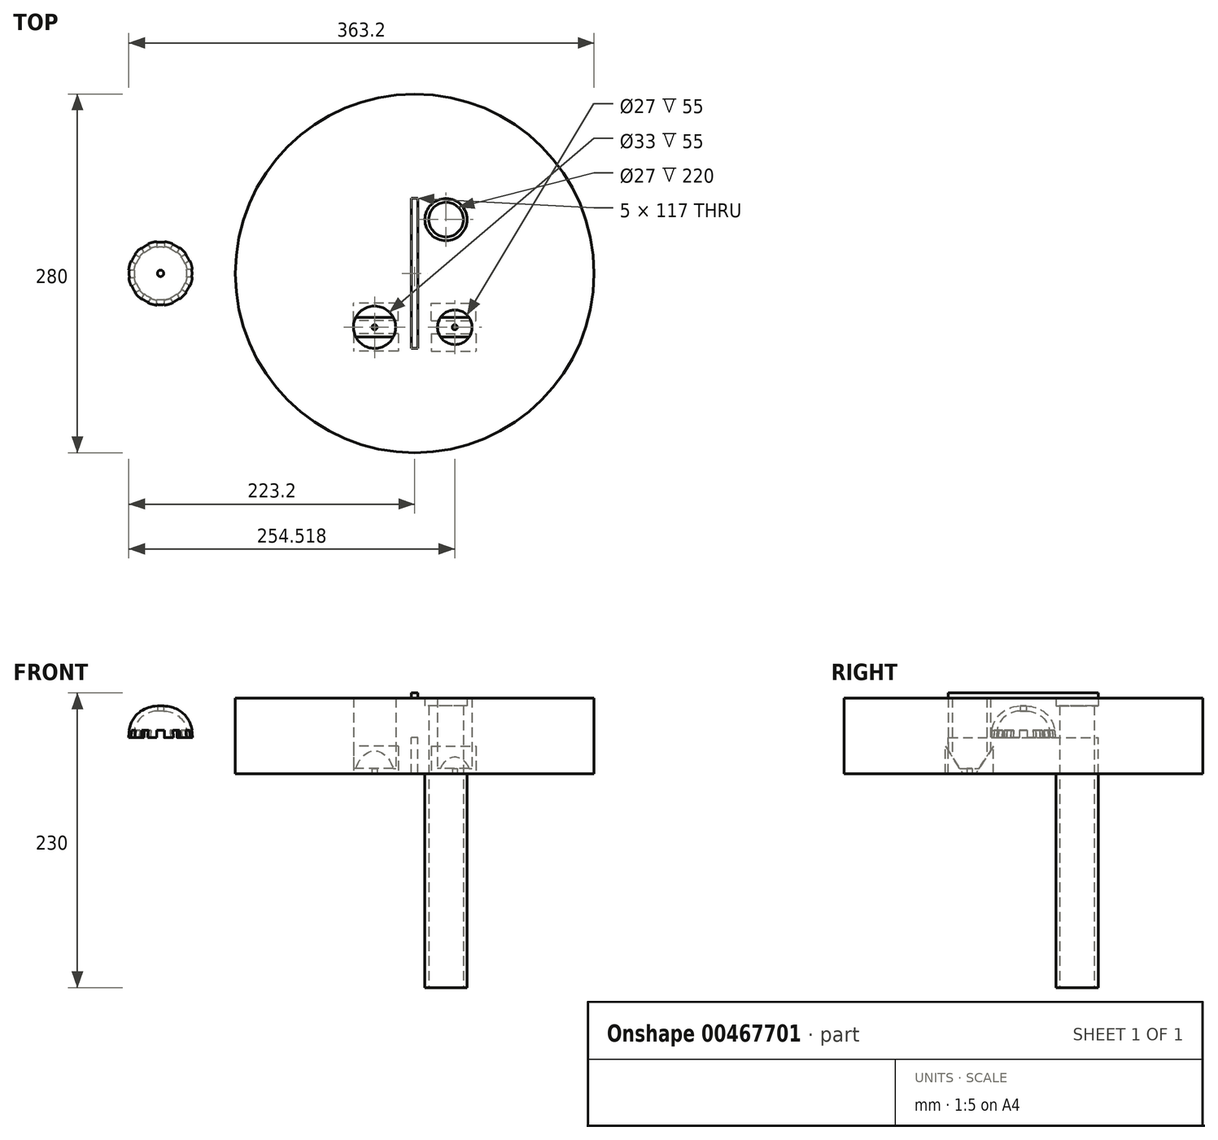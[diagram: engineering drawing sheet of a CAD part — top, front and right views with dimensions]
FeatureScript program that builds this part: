
annotation { "Feature Type Name" : "Feature", "Feature Type Description" : "" }
export const myFeature = defineFeature(function(context is Context, id is Id, definition is map)
    precondition{}
    {
        {
            var Q0;
            Q0=qCreatedBy(makeId("Top.planeOp"),FACE);
            var sketch = newSketch(context, id + "F0", { "sketchPlane" : qUnion([Q0])});
            skCircle(sketch, "E0", {"center": v(0, 0) * mm, "radius": 140 * mm});
            skLineSegment(sketch, "E1.bottom", {"start": v(2.5, -58.5) * mm, "end": v(-2.5, -58.5) * mm});
            skLineSegment(sketch, "E1.top", {"start": v(2.5, 58.5) * mm, "end": v(-2.5, 58.5) * mm});
            skLineSegment(sketch, "E1.left", {"start": v(2.5, -58.5) * mm, "end": v(2.5, 58.5) * mm});
            skLineSegment(sketch, "E1.right", {"start": v(-2.5, -58.5) * mm, "end": v(-2.5, 58.5) * mm});
            skLineSegment(sketch, "E2", {"start": v(-2.5, 0) * mm, "end": v(2.5, 0) * mm, "construction": true});
            skLineSegment(sketch, "E3", {"start": v(2.5, 58.5) * mm, "end": v(24.5, 58.5) * mm});
            skCircle(sketch, "E4", {"center": v(24.5, 42) * mm, "radius": 16.5 * mm});
            skLineSegment(sketch, "E5", {"start": v(2.5, -58.5) * mm, "end": v(32.5, -58.5) * mm, "construction": true});
            skCircle(sketch, "E6", {"center": v(31.32, -42.04) * mm, "radius": 16.5 * mm});
            skLineSegment(sketch, "E7", {"start": v(0, 58.5) * mm, "end": v(0, -58.5) * mm, "construction": true});
            skCircle(sketch, "E8.MirrorC", {"center": v(-31.32, -42.04) * mm, "radius": 16.5 * mm});
            skCircle(sketch, "E9.0", {"center": v(24.5, 42) * mm, "radius": 13.5 * mm});
            skCircle(sketch, "E10.0", {"center": v(31.32, -42.04) * mm, "radius": 13.5 * mm});
            skCircle(sketch, "E11.0", {"center": v(-31.32, -42.04) * mm, "radius": 13.5 * mm});
            skPoint(sketch, "E12", {"position": v(24.5, 58.5) * mm});
            skSolve(sketch);
        }
        {
            var Q0;
            Q0=makeQuery(id+"F0.imprint","IMPRINT",FACE,{"disambiguationData":[TD([[makeQuery(id+"F0.imprint","IMPRINT",EDGE,{"derivedFrom":sQuery(id+"F0.wireOp",EDGE,"E1.bottom")}),-1.0]])]});
            extrude(context, id + "F1", {"entities" : qUnion([Q0]), "depth" : 35 * mm, "offsetDistance" : 25 * mm});
        }
        {
            var Q0;
            Q0=makeQuery(id+"F0.imprint","IMPRINT",FACE,{"disambiguationData":[TD([[makeQuery(id+"F0.imprint","IMPRINT",EDGE,{"derivedFrom":sQuery(id+"F0.wireOp",EDGE,"E0")}),1.0]])]});
            extrude(context, id + "F2", {"entities" : qUnion([Q0]), "operationType" : NewBodyOperationType.ADD, "depth" : 5 * mm, "offsetDistance" : 25 * mm});
        }
        {
            var Q0;
            Q0=makeQuery(id+"F0.imprint","IMPRINT",FACE,{"disambiguationData":[TD([[makeQuery(id+"F0.imprint","IMPRINT",EDGE,{"derivedFrom":sQuery(id+"F0.wireOp",EDGE,"E4")}),1.0]])]});
            extrude(context, id + "F3", {"entities" : qUnion([Q0]), "operationType" : NewBodyOperationType.ADD, "depth" : 25 * mm, "offsetDistance" : 25 * mm});
        }
        {
            var Q0;
            Q0=makeQuery(id+"F0.imprint","IMPRINT",FACE,{"disambiguationData":[TD([[makeQuery(id+"F0.imprint","IMPRINT",EDGE,{"derivedFrom":sQuery(id+"F0.wireOp",EDGE,"E10.0")}),-1.0]])]});
            var Q1;
            Q1=makeQuery(id+"F0.imprint","IMPRINT",FACE,{"disambiguationData":[TD([[makeQuery(id+"F0.imprint","IMPRINT",EDGE,{"derivedFrom":sQuery(id+"F0.wireOp",EDGE,"E8.MirrorC")}),-1.0]])]});
            extrude(context, id + "F4", {"entities" : qUnion([Q0, Q1]), "operationType" : NewBodyOperationType.ADD, "depth" : 31 * mm, "offsetDistance" : 25 * mm});
        }
        {
            var Q0;
            Q0=makeQuery(id+"F0.imprint","IMPRINT",FACE,{"disambiguationData":[TD([[makeQuery(id+"F0.imprint","IMPRINT",EDGE,{"derivedFrom":sQuery(id+"F0.wireOp",EDGE,"E4")}),1.0]])]});
            extrude(context, id + "F5", {"entities" : qUnion([Q0]), "operationType" : NewBodyOperationType.ADD, "oppositeDirection" : true, "depth" : 195 * mm, "offsetDistance" : 25 * mm});
        }
        {
            var Q0;
            Q0=makeQuery(id+"F0.imprint","IMPRINT",FACE,{"disambiguationData":[TD([[makeQuery(id+"F0.imprint","IMPRINT",EDGE,{"derivedFrom":sQuery(id+"F0.wireOp",EDGE,"E10.0")}),-1.0]])]});
            var Q1;
            Q1=makeQuery(id+"F0.imprint","IMPRINT",FACE,{"disambiguationData":[TD([[makeQuery(id+"F0.imprint","IMPRINT",EDGE,{"derivedFrom":sQuery(id+"F0.wireOp",EDGE,"E8.MirrorC")}),-1.0]])]});
            extrude(context, id + "F6", {"entities" : qUnion([Q0, Q1]), "operationType" : NewBodyOperationType.ADD, "oppositeDirection" : true, "depth" : 28 * mm, "offsetDistance" : 25 * mm});
        }
        {
            var Q0;
            Q0=qCreatedBy(makeId("Front.planeOp"),FACE);
            var sketch = newSketch(context, id + "F7", { "sketchPlane" : qUnion([Q0])});
            skLineSegment(sketch, "E13", {"start": v(-198.37, 25) * mm, "end": v(-198.37, 0) * mm, "construction": true});
            skLineSegment(sketch, "E14", {"start": v(-198.37, 0) * mm, "end": v(-173.37, 0) * mm, "construction": true});
            skPoint(sketch, "E15.2.internal.snap0", {"position": v(-198.37, 12.5) * mm});
            skFitSpline(sketch, "E16", {"points": [v(-198.37, 25) * mm, v(-184.74, 21.83) * mm, v(-176.62, 13.93) * mm, v(-173.37, 0) * mm], "startDerivative": vector(48.6, -0.84) * mm, "endDerivative": vector(0.27, -46.68) * mm});
            skFitSpline(sketch, "E17.0", {"points": [v(-198.44, 21) * mm, v(-196.58, 20.97) * mm, v(-194.08, 20.75) * mm, v(-191.22, 20.15) * mm, v(-189.27, 19.54) * mm, v(-187.5, 18.79) * mm, v(-185.82, 17.87) * mm, v(-184.27, 16.8) * mm, v(-182.86, 15.56) * mm, v(-181.6, 14.2) * mm, v(-180.5, 12.68) * mm, v(-179.57, 11.03) * mm, v(-178.79, 9.2) * mm, v(-178.17, 7.17) * mm, v(-177.57, 4.22) * mm, v(-177.38, 1.74) * mm, v(-177.37, -0.02) * mm]});
            skLineSegment(sketch, "E18", {"start": v(-198.37, 25) * mm, "end": v(-198.37, 21) * mm});
            skLineSegment(sketch, "E19", {"start": v(-177.37, 0) * mm, "end": v(-173.37, 0) * mm});
            skSolve(sketch);
        }
        {
            var Q0;
            Q0=makeQuery(id+"F7.imprint","IMPRINT",FACE,{"disambiguationData":[TD([[makeQuery(id+"F7.imprint","IMPRINT",EDGE,{"derivedFrom":sQuery(id+"F7.wireOp",EDGE,"E16")}),-1.0]])]});
            var Q1;
            Q1=sQuery(id+"F7.wireOp",EDGE,"E13");
            revolve(context, id + "F8", {"entities" : qUnion([Q0]), "axis" : qUnion([Q1]), "revolveType" : RevolveType.FULL});
        }
        {
            var Q0;
            Q0=makeQuery(id+"F8.opRevolve","SWEPT_FACE",FACE,{"disambiguationData":[OSD([sQuery(id+"F7.wireOp",EDGE,"E19")])]});
            var sketch = newSketch(context, id + "F9", { "sketchPlane" : qUnion([Q0])});
            skLineSegment(sketch, "E20.bottom", {"start": v(-201.25, 34.28) * mm, "end": v(-195.25, 34.28) * mm});
            skLineSegment(sketch, "E20.top", {"start": v(-201.25, 17.44) * mm, "end": v(-195.25, 17.44) * mm});
            skLineSegment(sketch, "E20.left", {"start": v(-201.25, 34.28) * mm, "end": v(-201.25, 17.44) * mm});
            skLineSegment(sketch, "E20.right", {"start": v(-195.25, 34.28) * mm, "end": v(-195.25, 17.44) * mm});
            skLineSegment(sketch, "E21.1.0", {"start": v(-130.31, -157.15) * mm, "end": v(-127.31, -151.95) * mm});
            skLineSegment(sketch, "E21.1.1", {"start": v(-127.31, -151.95) * mm, "end": v(-112.73, -160.37) * mm});
            skLineSegment(sketch, "E21.1.2", {"start": v(-130.31, -157.15) * mm, "end": v(-115.73, -165.57) * mm});
            skLineSegment(sketch, "E21.1.3", {"start": v(-115.73, -165.57) * mm, "end": v(-112.73, -160.37) * mm});
            skLineSegment(sketch, "E21.2.0", {"start": v(70.94, -191.43) * mm, "end": v(67.94, -186.23) * mm});
            skLineSegment(sketch, "E21.2.1", {"start": v(67.94, -186.23) * mm, "end": v(82.52, -177.81) * mm});
            skLineSegment(sketch, "E21.2.2", {"start": v(70.94, -191.43) * mm, "end": v(85.52, -183.01) * mm});
            skLineSegment(sketch, "E21.2.3", {"start": v(85.52, -183.01) * mm, "end": v(82.52, -177.81) * mm});
            skPoint(sketch, "E21.center", {"position": v(0, 0) * mm});
            skLineSegment(sketch, "E22.1.3.0", {"start": v(201.25, -34.28) * mm, "end": v(195.25, -34.28) * mm});
            skLineSegment(sketch, "E22.3.3.0", {"start": v(195.25, -34.28) * mm, "end": v(195.25, -17.44) * mm});
            skLineSegment(sketch, "E22.6.3.0", {"start": v(201.25, -34.28) * mm, "end": v(201.25, -17.44) * mm});
            skLineSegment(sketch, "E22.9.3.0", {"start": v(201.25, -17.44) * mm, "end": v(195.25, -17.44) * mm});
            skLineSegment(sketch, "E22.1.4.0", {"start": v(130.31, 157.15) * mm, "end": v(127.31, 151.95) * mm});
            skLineSegment(sketch, "E22.3.4.0", {"start": v(127.31, 151.95) * mm, "end": v(112.73, 160.37) * mm});
            skLineSegment(sketch, "E22.6.4.0", {"start": v(130.31, 157.15) * mm, "end": v(115.73, 165.57) * mm});
            skLineSegment(sketch, "E22.9.4.0", {"start": v(115.73, 165.57) * mm, "end": v(112.73, 160.37) * mm});
            skLineSegment(sketch, "E22.1.5.0", {"start": v(-70.94, 191.43) * mm, "end": v(-67.94, 186.23) * mm});
            skLineSegment(sketch, "E22.3.5.0", {"start": v(-67.94, 186.23) * mm, "end": v(-82.52, 177.81) * mm});
            skLineSegment(sketch, "E22.6.5.0", {"start": v(-70.94, 191.43) * mm, "end": v(-85.52, 183.01) * mm});
            skLineSegment(sketch, "E22.9.5.0", {"start": v(-85.52, 183.01) * mm, "end": v(-82.52, 177.81) * mm});
            skSolve(sketch);
        }
        {
            var Q0;
            Q0=makeQuery(id+"F9.imprint","IMPRINT",FACE,{"disambiguationData":[TD([[makeQuery(id+"F9.imprint","IMPRINT",EDGE,{"derivedFrom":sQuery(id+"F9.wireOp",EDGE,"E21.1.0")}),-1.0]])]});
            var Q1;
            Q1=makeQuery(id+"F9.imprint","IMPRINT",FACE,{"disambiguationData":[TD([[makeQuery(id+"F9.imprint","IMPRINT",EDGE,{"derivedFrom":sQuery(id+"F9.wireOp",EDGE,"E21.2.0")}),-1.0]])]});
            var Q2;
            Q2=makeQuery(id+"F9.imprint","IMPRINT",FACE,{"disambiguationData":[TD([[makeQuery(id+"F9.imprint","IMPRINT",EDGE,{"derivedFrom":sQuery(id+"F9.wireOp",EDGE,"E22.1.3.0")}),-1.0]])]});
            var Q3;
            Q3=makeQuery(id+"F9.imprint","IMPRINT",FACE,{"disambiguationData":[TD([[makeQuery(id+"F9.imprint","IMPRINT",EDGE,{"derivedFrom":sQuery(id+"F9.wireOp",EDGE,"E22.1.4.0")}),-1.0]])]});
            var Q4;
            Q4=makeQuery(id+"F9.imprint","IMPRINT",FACE,{"disambiguationData":[TD([[makeQuery(id+"F9.imprint","IMPRINT",EDGE,{"derivedFrom":sQuery(id+"F9.wireOp",EDGE,"E22.1.5.0")}),-1.0]])]});
            var Q5;
            {var subQ0=sQuery(id+"F9.wireOp",EDGE,"E20.left");var subQ1=sQuery(id+"F7.wireOp",EDGE,"E19");var subQ2=makeQuery(id+"F8.opRevolve","SWEPT_EDGE",EDGE,{"disambiguationData":[OSD([sQuery(id+"F7.wireOp",EDGE,"E16"),subQ1])]});var subQ3=makeQuery(id+"F9.imprint","INTERSECT",VERTEX,{"derivedFrom":[subQ2,subQ0]});Q5=makeQuery(id+"F9.imprint","IMPRINT",FACE,{"disambiguationData":[TD([[makeQuery(id+"F9.imprint","IMPRINT",EDGE,{"disambiguationData":[TD([[subQ3,-1.0]])],"derivedFrom":subQ0}),1.0]])]});}
            var Q6;
            {var subQ0=sQuery(id+"F9.wireOp",EDGE,"E20.top");Q6=makeQuery(id+"F9.imprint","IMPRINT",FACE,{"disambiguationData":[TD([[makeQuery(id+"F9.imprint","IMPRINT",EDGE,{"derivedFrom":subQ0}),1.0]])]});}
            var Q7;
            {var subQ0=sQuery(id+"F9.wireOp",EDGE,"E20.bottom");Q7=makeQuery(id+"F9.imprint","IMPRINT",FACE,{"disambiguationData":[TD([[makeQuery(id+"F9.imprint","IMPRINT",EDGE,{"derivedFrom":subQ0}),-1.0]])]});}
            extrude(context, id + "F10", {"entities" : qUnion([Q0, Q1, Q2, Q3, Q4, Q5, Q6, Q7]), "oppositeDirection" : true, "depth" : 6 * mm, "offsetDistance" : 25 * mm});
        }
        {
            var Q0;
            Q0=makeQuery(id+"F10.opExtrude","SWEPT_BODY",BODY,{"disambiguationData":[OSD([sQuery(id+"F9.wireOp",EDGE,"E20.bottom"),sQuery(id+"F9.wireOp",EDGE,"E20.top"),sQuery(id+"F9.wireOp",EDGE,"E20.left"),sQuery(id+"F9.wireOp",EDGE,"E20.right")])]});
            var Q1;
            Q1=sQuery(id+"F7.wireOp",EDGE,"E13");
            circularPattern(context, id + "F11", {"entities" : qUnion([Q0]), "axis" : qUnion([Q1]), "angle" : 360 * degree, "instanceCount" : 12, "equalSpace" : true});
        }
        {
            var Q0;
            Q0=makeQuery(id+"F11.opPattern","COPY",BODY,{"derivedFrom":makeQuery(id+"F10.opExtrude","SWEPT_BODY",BODY,{"disambiguationData":[OSD([sQuery(id+"F9.wireOp",EDGE,"E20.bottom"),sQuery(id+"F9.wireOp",EDGE,"E20.top"),sQuery(id+"F9.wireOp",EDGE,"E20.left"),sQuery(id+"F9.wireOp",EDGE,"E20.right")])]}),"instanceName":"4"});
            var Q1;
            Q1=makeQuery(id+"F11.opPattern","COPY",BODY,{"derivedFrom":makeQuery(id+"F10.opExtrude","SWEPT_BODY",BODY,{"disambiguationData":[OSD([sQuery(id+"F9.wireOp",EDGE,"E20.bottom"),sQuery(id+"F9.wireOp",EDGE,"E20.top"),sQuery(id+"F9.wireOp",EDGE,"E20.left"),sQuery(id+"F9.wireOp",EDGE,"E20.right")])]}),"instanceName":"3"});
            var Q2;
            Q2=makeQuery(id+"F11.opPattern","COPY",BODY,{"derivedFrom":makeQuery(id+"F10.opExtrude","SWEPT_BODY",BODY,{"disambiguationData":[OSD([sQuery(id+"F9.wireOp",EDGE,"E20.bottom"),sQuery(id+"F9.wireOp",EDGE,"E20.top"),sQuery(id+"F9.wireOp",EDGE,"E20.left"),sQuery(id+"F9.wireOp",EDGE,"E20.right")])]}),"instanceName":"2"});
            var Q3;
            Q3=makeQuery(id+"F11.opPattern","COPY",BODY,{"derivedFrom":makeQuery(id+"F10.opExtrude","SWEPT_BODY",BODY,{"disambiguationData":[OSD([sQuery(id+"F9.wireOp",EDGE,"E20.bottom"),sQuery(id+"F9.wireOp",EDGE,"E20.top"),sQuery(id+"F9.wireOp",EDGE,"E20.left"),sQuery(id+"F9.wireOp",EDGE,"E20.right")])]}),"instanceName":"1"});
            var Q4;
            Q4=makeQuery(id+"F10.opExtrude","SWEPT_BODY",BODY,{"disambiguationData":[OSD([sQuery(id+"F9.wireOp",EDGE,"E20.bottom"),sQuery(id+"F9.wireOp",EDGE,"E20.top"),sQuery(id+"F9.wireOp",EDGE,"E20.left"),sQuery(id+"F9.wireOp",EDGE,"E20.right")])]});
            var Q5;
            Q5=makeQuery(id+"F11.opPattern","COPY",BODY,{"derivedFrom":makeQuery(id+"F10.opExtrude","SWEPT_BODY",BODY,{"disambiguationData":[OSD([sQuery(id+"F9.wireOp",EDGE,"E20.bottom"),sQuery(id+"F9.wireOp",EDGE,"E20.top"),sQuery(id+"F9.wireOp",EDGE,"E20.left"),sQuery(id+"F9.wireOp",EDGE,"E20.right")])]}),"instanceName":"11"});
            var Q6;
            Q6=makeQuery(id+"F11.opPattern","COPY",BODY,{"derivedFrom":makeQuery(id+"F10.opExtrude","SWEPT_BODY",BODY,{"disambiguationData":[OSD([sQuery(id+"F9.wireOp",EDGE,"E20.bottom"),sQuery(id+"F9.wireOp",EDGE,"E20.top"),sQuery(id+"F9.wireOp",EDGE,"E20.left"),sQuery(id+"F9.wireOp",EDGE,"E20.right")])]}),"instanceName":"10"});
            var Q7;
            Q7=makeQuery(id+"F11.opPattern","COPY",BODY,{"derivedFrom":makeQuery(id+"F10.opExtrude","SWEPT_BODY",BODY,{"disambiguationData":[OSD([sQuery(id+"F9.wireOp",EDGE,"E20.bottom"),sQuery(id+"F9.wireOp",EDGE,"E20.top"),sQuery(id+"F9.wireOp",EDGE,"E20.left"),sQuery(id+"F9.wireOp",EDGE,"E20.right")])]}),"instanceName":"9"});
            var Q8;
            Q8=makeQuery(id+"F11.opPattern","COPY",BODY,{"derivedFrom":makeQuery(id+"F10.opExtrude","SWEPT_BODY",BODY,{"disambiguationData":[OSD([sQuery(id+"F9.wireOp",EDGE,"E20.bottom"),sQuery(id+"F9.wireOp",EDGE,"E20.top"),sQuery(id+"F9.wireOp",EDGE,"E20.left"),sQuery(id+"F9.wireOp",EDGE,"E20.right")])]}),"instanceName":"8"});
            var Q9;
            Q9=makeQuery(id+"F11.opPattern","COPY",BODY,{"derivedFrom":makeQuery(id+"F10.opExtrude","SWEPT_BODY",BODY,{"disambiguationData":[OSD([sQuery(id+"F9.wireOp",EDGE,"E20.bottom"),sQuery(id+"F9.wireOp",EDGE,"E20.top"),sQuery(id+"F9.wireOp",EDGE,"E20.left"),sQuery(id+"F9.wireOp",EDGE,"E20.right")])]}),"instanceName":"7"});
            var Q10;
            Q10=makeQuery(id+"F11.opPattern","COPY",BODY,{"derivedFrom":makeQuery(id+"F10.opExtrude","SWEPT_BODY",BODY,{"disambiguationData":[OSD([sQuery(id+"F9.wireOp",EDGE,"E20.bottom"),sQuery(id+"F9.wireOp",EDGE,"E20.top"),sQuery(id+"F9.wireOp",EDGE,"E20.left"),sQuery(id+"F9.wireOp",EDGE,"E20.right")])]}),"instanceName":"6"});
            var Q11;
            Q11=makeQuery(id+"F11.opPattern","COPY",BODY,{"derivedFrom":makeQuery(id+"F10.opExtrude","SWEPT_BODY",BODY,{"disambiguationData":[OSD([sQuery(id+"F9.wireOp",EDGE,"E20.bottom"),sQuery(id+"F9.wireOp",EDGE,"E20.top"),sQuery(id+"F9.wireOp",EDGE,"E20.left"),sQuery(id+"F9.wireOp",EDGE,"E20.right")])]}),"instanceName":"5"});
            var Q12;
            Q12=makeQuery(id+"F8.opRevolve","SWEPT_BODY",BODY,{"disambiguationData":[OSD([sQuery(id+"F7.wireOp",EDGE,"E16"),sQuery(id+"F7.wireOp",EDGE,"E17.0"),sQuery(id+"F7.wireOp",EDGE,"E18"),sQuery(id+"F7.wireOp",EDGE,"E19")])]});
            booleanBodies(context, id + "F12", {"operationType" : BooleanOperationType.SUBTRACTION, "tools" : qUnion([Q0, Q1, Q2, Q3, Q4, Q5, Q6, Q7, Q8, Q9, Q10, Q11]), "targets" : qUnion([Q12])});
        }
        {
            var Q0;
            Q0=sQuery(id+"F7.wireOp",EDGE,"E14");
            cPlane(context, id + "F13", {"entities" : qUnion([Q0]), "cplaneType" : CPlaneType.LINE_ANGLE, "offset" : 25 * mm, "angle" : 90 * degree, "width" : 150 * mm, "height" : 150 * mm});
        }
        {
            var Q0;
            Q0=qCreatedBy(id+"F13.planeOp",FACE);
            var sketch = newSketch(context, id + "F14", { "sketchPlane" : qUnion([Q0])});
            skCircle(sketch, "E23", {"center": v(-198.37, 0) * mm, "radius": 2.5 * mm});
            skSolve(sketch);
        }
        {
            var Q0;
            Q0=makeQuery(id+"F14.imprint","IMPRINT",FACE,{"disambiguationData":[TD([[makeQuery(id+"F14.imprint","IMPRINT",EDGE,{"derivedFrom":sQuery(id+"F14.wireOp",EDGE,"E23")}),1.0]])]});
            extrude(context, id + "F15", {"entities" : qUnion([Q0]), "operationType" : NewBodyOperationType.REMOVE, "depth" : 30 * mm, "offsetDistance" : 25 * mm});
        }
        {
            var Q0;
            Q0=makeQuery(id+"F10.opExtrude","SWEPT_BODY",BODY,{"disambiguationData":[OSD([sQuery(id+"F9.wireOp",EDGE,"E21.1.0"),sQuery(id+"F9.wireOp",EDGE,"E21.1.1"),sQuery(id+"F9.wireOp",EDGE,"E21.1.2"),sQuery(id+"F9.wireOp",EDGE,"E21.1.3")])]});
            var Q1;
            Q1=makeQuery(id+"F10.opExtrude","SWEPT_BODY",BODY,{"disambiguationData":[OSD([sQuery(id+"F9.wireOp",EDGE,"E21.2.0"),sQuery(id+"F9.wireOp",EDGE,"E21.2.1"),sQuery(id+"F9.wireOp",EDGE,"E21.2.2"),sQuery(id+"F9.wireOp",EDGE,"E21.2.3")])]});
            var Q2;
            Q2=makeQuery(id+"F10.opExtrude","SWEPT_BODY",BODY,{"disambiguationData":[OSD([sQuery(id+"F9.wireOp",EDGE,"E22.1.3.0"),sQuery(id+"F9.wireOp",EDGE,"E22.3.3.0"),sQuery(id+"F9.wireOp",EDGE,"E22.6.3.0"),sQuery(id+"F9.wireOp",EDGE,"E22.9.3.0")])]});
            var Q3;
            Q3=makeQuery(id+"F10.opExtrude","SWEPT_BODY",BODY,{"disambiguationData":[OSD([sQuery(id+"F9.wireOp",EDGE,"E22.1.4.0"),sQuery(id+"F9.wireOp",EDGE,"E22.3.4.0"),sQuery(id+"F9.wireOp",EDGE,"E22.6.4.0"),sQuery(id+"F9.wireOp",EDGE,"E22.9.4.0")])]});
            var Q4;
            Q4=makeQuery(id+"F10.opExtrude","SWEPT_BODY",BODY,{"disambiguationData":[OSD([sQuery(id+"F9.wireOp",EDGE,"E22.1.5.0"),sQuery(id+"F9.wireOp",EDGE,"E22.3.5.0"),sQuery(id+"F9.wireOp",EDGE,"E22.6.5.0"),sQuery(id+"F9.wireOp",EDGE,"E22.9.5.0")])]});
            deleteBodies(context, id + "F16", {"entities" : qUnion([Q0, Q1, Q2, Q3, Q4])});
        }
        {
            var Q0;
            Q0=makeQuery(id+"F6.opExtrude","CAP_FACE",FACE,{"disambiguationData":[OSD([sQuery(id+"F0.wireOp",EDGE,"E8.MirrorC"),sQuery(id+"F0.wireOp",EDGE,"E11.0")])],"isStart":false});
            var sketch = newSketch(context, id + "F17", { "sketchPlane" : qUnion([Q0])});
            skCircle(sketch, "E24.0", {"center": v(-31.32, 42.04) * mm, "radius": 16.5 * mm});
            skCircle(sketch, "E25", {"center": v(-31.32, 42.04) * mm, "radius": 2 * mm});
            skSolve(sketch);
        }
        {
            var Q0;
            Q0 = qSketchRegion(id + "F17", true);
            extrude(context, id + "F18", {"entities" : qUnion([Q0]), "operationType" : NewBodyOperationType.ADD, "oppositeDirection" : true, "depth" : 4 * mm, "offsetDistance" : 25 * mm});
        }
        {
            var Q0;
            Q0=makeQuery(id+"F6.opExtrude","CAP_FACE",FACE,{"disambiguationData":[OSD([sQuery(id+"F0.wireOp",EDGE,"E6"),sQuery(id+"F0.wireOp",EDGE,"E10.0")])],"isStart":false});
            var sketch = newSketch(context, id + "F19", { "sketchPlane" : qUnion([Q0])});
            skCircle(sketch, "E26.0", {"center": v(31.32, 42.04) * mm, "radius": 16.5 * mm});
            skCircle(sketch, "E27", {"center": v(31.32, 42.04) * mm, "radius": 2 * mm});
            skSolve(sketch);
        }
        {
            var Q0;
            Q0 = qSketchRegion(id + "F19", true);
            extrude(context, id + "F20", {"entities" : qUnion([Q0]), "operationType" : NewBodyOperationType.ADD, "oppositeDirection" : true, "depth" : 4 * mm, "offsetDistance" : 25 * mm});
        }
        {
            var Q0;
            Q0=makeQuery(id+"F18.boolean.opBoolean","MERGE",FACE,{"derivedFrom":[makeQuery(id+"F6.opExtrude","CAP_FACE",FACE,{"disambiguationData":[OSD([sQuery(id+"F0.wireOp",EDGE,"E8.MirrorC"),sQuery(id+"F0.wireOp",EDGE,"E11.0")])],"isStart":false}),makeQuery(id+"F18.opExtrude","CAP_FACE",FACE,{"disambiguationData":[OSD([sQuery(id+"F17.wireOp",EDGE,"E24.0"),sQuery(id+"F17.wireOp",EDGE,"E25")])],"isStart":true})]});
            var sketch = newSketch(context, id + "F21", { "sketchPlane" : qUnion([Q0])});
            skCircle(sketch, "E28.0", {"center": v(-31.32, 42.04) * mm, "radius": 16.5 * mm});
            skLineSegment(sketch, "E29", {"start": v(-47.82, 42.04) * mm, "end": v(-14.82, 42.04) * mm});
            skLineSegment(sketch, "E30", {"start": v(-47.82, 47.04) * mm, "end": v(-14.82, 47.04) * mm});
            skLineSegment(sketch, "E31.top", {"start": v(-47.82, 60.87) * mm, "end": v(-14.82, 60.87) * mm});
            skLineSegment(sketch, "E31.left", {"start": v(-47.82, 47.04) * mm, "end": v(-47.82, 60.87) * mm});
            skLineSegment(sketch, "E31.right", {"start": v(-14.82, 47.04) * mm, "end": v(-14.82, 60.87) * mm});
            skSolve(sketch);
        }
        {
            var Q0;
            Q0=sQuery(id+"F21.wireOp",EDGE,"E31.left");
            cPlane(context, id + "F22", {"entities" : qUnion([Q0]), "cplaneType" : CPlaneType.LINE_ANGLE, "offset" : 25 * mm, "angle" : 90 * degree, "width" : 150 * mm, "height" : 150 * mm});
        }
        {
            var Q0;
            Q0=qCreatedBy(id+"F22.planeOp",FACE);
            var sketch = newSketch(context, id + "F23", { "sketchPlane" : qUnion([Q0])});
            skLineSegment(sketch, "E32.0", {"start": v(-47.04, -28) * mm, "end": v(-60.87, -28) * mm});
            skLineSegment(sketch, "E33", {"start": v(-60.87, -28) * mm, "end": v(-60.87, -6.5) * mm});
            skLineSegment(sketch, "E34", {"start": v(-60.87, -6.5) * mm, "end": v(-47.04, -28) * mm});
            skLineSegment(sketch, "E35.0", {"start": v(-140, 0) * mm, "end": v(140, 0) * mm});
            skLineSegment(sketch, "E36", {"start": v(-25.54, 0) * mm, "end": v(-25.54, -28) * mm});
            skLineSegment(sketch, "E37", {"start": v(-58.54, -28) * mm, "end": v(-58.54, -0.03) * mm});
            skLineSegment(sketch, "E38", {"start": v(-58.54, -28) * mm, "end": v(-58.54, 0) * mm});
            skPoint(sketch, "E39", {"position": v(-58.54, -10.03) * mm});
            skSolve(sketch);
        }
        {
            var Q0;
            Q0 = qSketchRegion(id + "F23", true);
            extrude(context, id + "F24", {"entities" : qUnion([Q0]), "depth" : 35 * mm, "offsetDistance" : 25 * mm});
        }
        {
            var Q0;
            Q0=sQuery(id+"F21.wireOp",EDGE,"E29");
            cPlane(context, id + "F25", {"entities" : qUnion([Q0]), "cplaneType" : CPlaneType.LINE_ANGLE, "offset" : 25 * mm, "angle" : 0 * degree, "width" : 150 * mm, "height" : 150 * mm});
        }
        {
            var Q0;
            Q0=makeQuery(id+"F24.opExtrude","SWEPT_BODY",BODY,{"disambiguationData":[OSD([sQuery(id+"F23.wireOp",EDGE,"E32.0"),sQuery(id+"F23.wireOp",EDGE,"E33"),sQuery(id+"F23.wireOp",EDGE,"E34")])]});
            var Q1;
            Q1=qCreatedBy(id+"F25.planeOp",FACE);
            mirror(context, id + "F26", {"entities" : qUnion([Q0]), "mirrorPlane" : qUnion([Q1])});
        }
        {
            var Q0;
            Q0=makeQuery(id+"F26.opPattern","COPY",BODY,{"derivedFrom":makeQuery(id+"F24.opExtrude","SWEPT_BODY",BODY,{"disambiguationData":[OSD([sQuery(id+"F23.wireOp",EDGE,"E32.0"),sQuery(id+"F23.wireOp",EDGE,"E33"),sQuery(id+"F23.wireOp",EDGE,"E34")])]}),"instanceName":"1"});
            var Q1;
            Q1=makeQuery(id+"F24.opExtrude","SWEPT_BODY",BODY,{"disambiguationData":[OSD([sQuery(id+"F23.wireOp",EDGE,"E32.0"),sQuery(id+"F23.wireOp",EDGE,"E33"),sQuery(id+"F23.wireOp",EDGE,"E34")])]});
            var Q2;
            Q2=qCreatedBy(makeId("Right.planeOp"),FACE);
            mirror(context, id + "F27", {"operationType" : NewBodyOperationType.REMOVE, "entities" : qUnion([Q0, Q1]), "mirrorPlane" : qUnion([Q2])});
        }
        {
            var Q0;
            Q0=makeQuery(id+"F26.opPattern","COPY",BODY,{"derivedFrom":makeQuery(id+"F24.opExtrude","SWEPT_BODY",BODY,{"disambiguationData":[OSD([sQuery(id+"F23.wireOp",EDGE,"E32.0"),sQuery(id+"F23.wireOp",EDGE,"E33"),sQuery(id+"F23.wireOp",EDGE,"E34")])]}),"instanceName":"1"});
            var Q1;
            Q1=makeQuery(id+"F24.opExtrude","SWEPT_BODY",BODY,{"disambiguationData":[OSD([sQuery(id+"F23.wireOp",EDGE,"E32.0"),sQuery(id+"F23.wireOp",EDGE,"E33"),sQuery(id+"F23.wireOp",EDGE,"E34")])]});
            var Q2;
            Q2=makeQuery(id+"F1.opExtrude","SWEPT_BODY",BODY,{"disambiguationData":[OSD([sQuery(id+"F0.wireOp",EDGE,"E1.bottom"),sQuery(id+"F0.wireOp",EDGE,"E1.top"),sQuery(id+"F0.wireOp",EDGE,"E1.left"),sQuery(id+"F0.wireOp",EDGE,"E1.right")])]});
            booleanBodies(context, id + "F28", {"operationType" : BooleanOperationType.SUBTRACTION, "tools" : qUnion([Q0, Q1]), "targets" : qUnion([Q2])});
        }
    });
